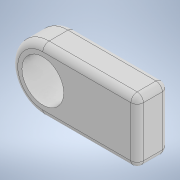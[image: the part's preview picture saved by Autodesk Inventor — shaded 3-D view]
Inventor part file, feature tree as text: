
AUTODESK INVENTOR PART (.ipt)
format: ipt  version: 2021.1 (Build 251245010, 245A)  size: 130,048 bytes
history: native  units: mm
features: extrude x1, fillet x1, sketch x1
ambient origin geometry x8: Origin, YZ Plane, XZ Plane, XY Plane, X Axis, Y Axis, Z Axis, Center Point
bodies: Solid1 (feature_tree)
feature tree (3):
  extrude  "Extrusion1"  Depth=20.0mm
  fillet  "Fillet1"  Radius=30.0mm
  sketch  "Sketch1"  dims[d0=13.3mm d2=20.0mm d3=30.0mm d4=20.0mm d5=10.0mm d6=0.0mm d7=2.0mm]
